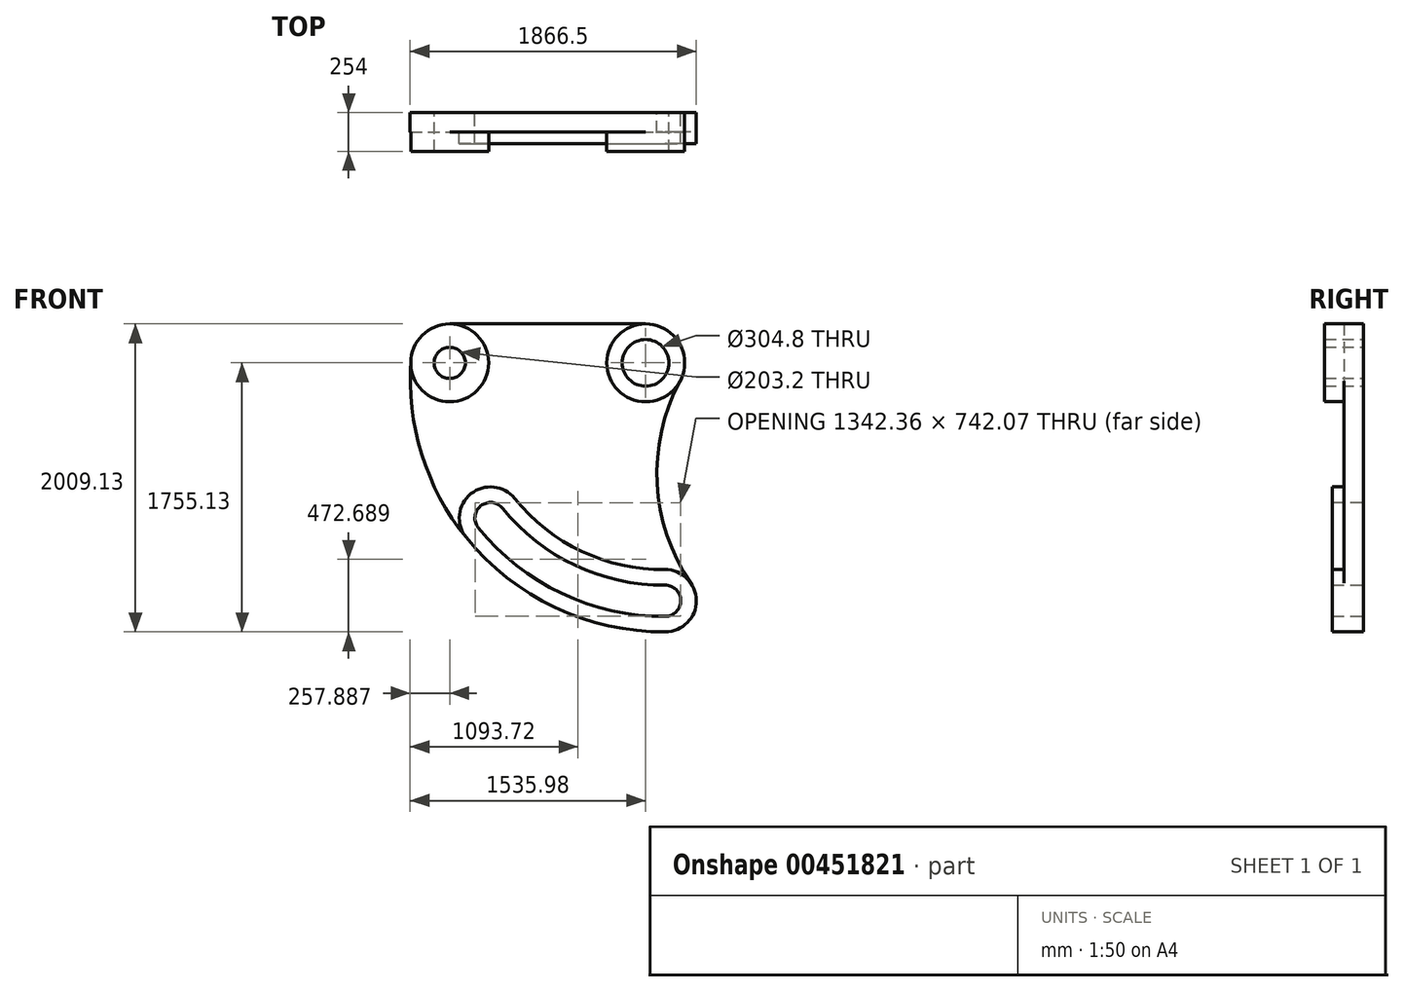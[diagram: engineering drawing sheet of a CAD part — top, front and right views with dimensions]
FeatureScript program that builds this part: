
annotation { "Feature Type Name" : "Feature", "Feature Type Description" : "" }
export const myFeature = defineFeature(function(context is Context, id is Id, definition is map)
    precondition{}
    {
        {
            var Q0;
            Q0=qCreatedBy(makeId("Front.planeOp"),FACE);
            var sketch = newSketch(context, id + "F0", { "sketchPlane" : qUnion([Q0])});
            skLineSegment(sketch, "E0", {"start": v(0, 0) * mm, "end": v(-1278.1, 0) * mm});
            skCircle(sketch, "E1", {"center": v(0, -254) * mm, "radius": 254 * mm});
            skCircle(sketch, "E2", {"center": v(0, -254) * mm, "radius": 152.4 * mm});
            skCircle(sketch, "E3", {"center": v(-1278.1, -254) * mm, "radius": 254 * mm});
            skCircle(sketch, "E4", {"center": v(-1278.1, -254) * mm, "radius": 101.6 * mm});
            skArc(sketch, "E5", {"start": v(128.19, -1907.48) * mm, "mid": v(228.92, -1805.02) * mm, "end": v(126.46, -1704.28) * mm});
            skArc(sketch, "E6", {"start": v(223.86, -374) * mm, "mid": v(75.04, -1042.53) * mm, "end": v(295.03, -1691.14) * mm});
            skArc(sketch, "E7", {"start": v(-1531.39, -235.07) * mm, "mid": v(-1090.36, -1486.34) * mm, "end": v(129.05, -2009.07) * mm});
            skArc(sketch, "E8", {"start": v(-933.3, -1202.68) * mm, "mid": v(-1076.16, -1187.3) * mm, "end": v(-1091.54, -1330.16) * mm});
            skArc(sketch, "E9", {"start": v(-854.19, -1138.94) * mm, "mid": v(-1139.9, -1108.19) * mm, "end": v(-1170.66, -1393.9) * mm});
            skArc(sketch, "E10.0", {"start": v(-1091.54, -1330.16) * mm, "mid": v(-547.83, -1758.58) * mm, "end": v(128.19, -1907.48) * mm});
            skArc(sketch, "E11.0", {"start": v(-933.3, -1202.68) * mm, "mid": v(-460.9, -1574.92) * mm, "end": v(126.46, -1704.28) * mm});
            skArc(sketch, "E12.trimOffspring", {"start": v(-854.19, -1138.94) * mm, "mid": v(-417.43, -1483.09) * mm, "end": v(125.6, -1602.69) * mm});
            skArc(sketch, "E13.trimOffspring", {"start": v(129.05, -2009.07) * mm, "mid": v(330.51, -1804.15) * mm, "end": v(125.6, -1602.69) * mm});
            skSolve(sketch);
        }
        {
            var Q0;
            {var subQ0=sQuery(id+"F0.wireOp",EDGE,"E6");Q0=makeQuery(id+"F0.imprint","IMPRINT",FACE,{"disambiguationData":[TD([[makeQuery(id+"F0.imprint","IMPRINT",EDGE,{"derivedFrom":subQ0}),-1.0]])]});}
            extrude(context, id + "F1", {"entities" : qUnion([Q0]), "depth" : 127 * mm});
        }
        {
            var Q0;
            Q0=makeQuery(id+"F0.imprint","IMPRINT",FACE,{"disambiguationData":[TD([[makeQuery(id+"F0.imprint","IMPRINT",EDGE,{"derivedFrom":sQuery(id+"F0.wireOp",EDGE,"E5")}),-1.0]])]});
            extrude(context, id + "F2", {"entities" : qUnion([Q0]), "operationType" : NewBodyOperationType.ADD, "depth" : 203.2 * mm});
        }
        {
            var Q0;
            Q0=makeQuery(id+"F0.imprint","IMPRINT",FACE,{"disambiguationData":[TD([[makeQuery(id+"F0.imprint","IMPRINT",EDGE,{"derivedFrom":sQuery(id+"F0.wireOp",EDGE,"E4")}),-1.0]])]});
            var Q1;
            Q1=makeQuery(id+"F0.imprint","IMPRINT",FACE,{"disambiguationData":[TD([[makeQuery(id+"F0.imprint","IMPRINT",EDGE,{"derivedFrom":sQuery(id+"F0.wireOp",EDGE,"E2")}),-1.0]])]});
            extrude(context, id + "F3", {"entities" : qUnion([Q0, Q1]), "operationType" : NewBodyOperationType.ADD, "depth" : 254 * mm});
        }
    });
